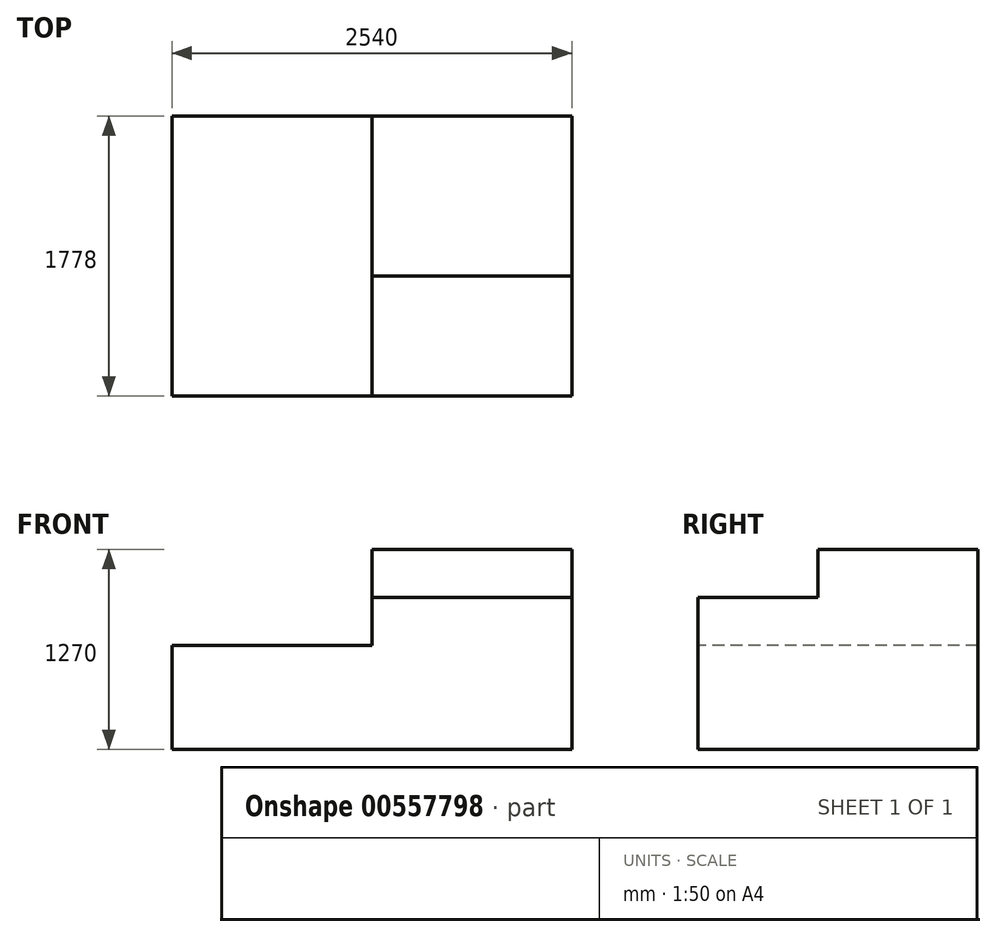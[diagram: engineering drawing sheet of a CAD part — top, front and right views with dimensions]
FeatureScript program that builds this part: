
annotation { "Feature Type Name" : "Feature", "Feature Type Description" : "" }
export const myFeature = defineFeature(function(context is Context, id is Id, definition is map)
    precondition{}
    {
        {
            var Q0;
            Q0=qCreatedBy(makeId("Front.planeOp"),FACE);
            var sketch = newSketch(context, id + "F0", { "sketchPlane" : qUnion([Q0])});
            skLineSegment(sketch, "E0", {"start": v(-1127.1, -27.42) * mm, "end": v(1412.9, -27.42) * mm});
            skLineSegment(sketch, "E1", {"start": v(1412.9, -27.42) * mm, "end": v(1412.9, 937.78) * mm});
            skLineSegment(sketch, "E2", {"start": v(1412.9, 937.78) * mm, "end": v(142.9, 937.78) * mm});
            skLineSegment(sketch, "E3", {"start": v(142.9, 937.78) * mm, "end": v(142.9, 632.98) * mm});
            skLineSegment(sketch, "E4", {"start": v(142.9, 632.98) * mm, "end": v(-1127.1, 632.98) * mm});
            skLineSegment(sketch, "E5", {"start": v(-1127.1, 632.98) * mm, "end": v(-1127.1, -27.42) * mm});
            skSolve(sketch);
        }
        {
            var Q0;
            Q0=makeQuery(id+"F0.imprint","IMPRINT",FACE,{"disambiguationData":[TD([[makeQuery(id+"F0.imprint","IMPRINT",EDGE,{"derivedFrom":sQuery(id+"F0.wireOp",EDGE,"E0")}),1.0]])]});
            extrude(context, id + "F1", {"entities" : qUnion([Q0]), "oppositeDirection" : true, "depth" : 762 * mm, "offsetDistance" : 25.4 * mm});
        }
        {
            var Q0;
            Q0=makeQuery(id+"F1.opExtrude","CAP_FACE",FACE,{"disambiguationData":[OSD([sQuery(id+"F0.wireOp",EDGE,"E0"),sQuery(id+"F0.wireOp",EDGE,"E1"),sQuery(id+"F0.wireOp",EDGE,"E2"),sQuery(id+"F0.wireOp",EDGE,"E3"),sQuery(id+"F0.wireOp",EDGE,"E4"),sQuery(id+"F0.wireOp",EDGE,"E5")])],"isStart":false});
            var sketch = newSketch(context, id + "F2", { "sketchPlane" : qUnion([Q0])});
            skLineSegment(sketch, "E6", {"start": v(-142.9, 937.78) * mm, "end": v(-142.9, 1242.58) * mm});
            skLineSegment(sketch, "E7", {"start": v(-142.9, 1242.58) * mm, "end": v(-1412.9, 1242.58) * mm});
            skLineSegment(sketch, "E8", {"start": v(-1412.9, 1242.58) * mm, "end": v(-1412.9, 937.78) * mm});
            skLineSegment(sketch, "E9", {"start": v(-1412.9, 937.78) * mm, "end": v(-1412.9, -27.42) * mm});
            skLineSegment(sketch, "E10", {"start": v(-1412.9, -27.42) * mm, "end": v(1127.1, -27.42) * mm});
            skLineSegment(sketch, "E11", {"start": v(1127.1, -27.42) * mm, "end": v(1127.1, 632.98) * mm});
            skLineSegment(sketch, "E12", {"start": v(1127.1, 632.98) * mm, "end": v(-142.9, 632.98) * mm});
            skLineSegment(sketch, "E13", {"start": v(-142.9, 632.98) * mm, "end": v(-142.9, 937.78) * mm});
            skSolve(sketch);
        }
        {
            var Q0;
            Q0=makeQuery(id+"F2.imprint","IMPRINT",FACE,{"disambiguationData":[TD([[makeQuery(id+"F2.imprint","IMPRINT",EDGE,{"derivedFrom":sQuery(id+"F2.wireOp",EDGE,"E6")}),1.0]])]});
            var Q1;
            Q1=makeQuery(id+"F2.imprint","IMPRINT",FACE,{"disambiguationData":[TD([[makeQuery(id+"F2.imprint","IMPRINT",EDGE,{"derivedFrom":sQuery(id+"F2.wireOp",EDGE,"E9")}),-1.0]])]});
            extrude(context, id + "F3", {"entities" : qUnion([Q0, Q1]), "operationType" : NewBodyOperationType.ADD, "depth" : 1016 * mm, "offsetDistance" : 25.4 * mm});
        }
    });
